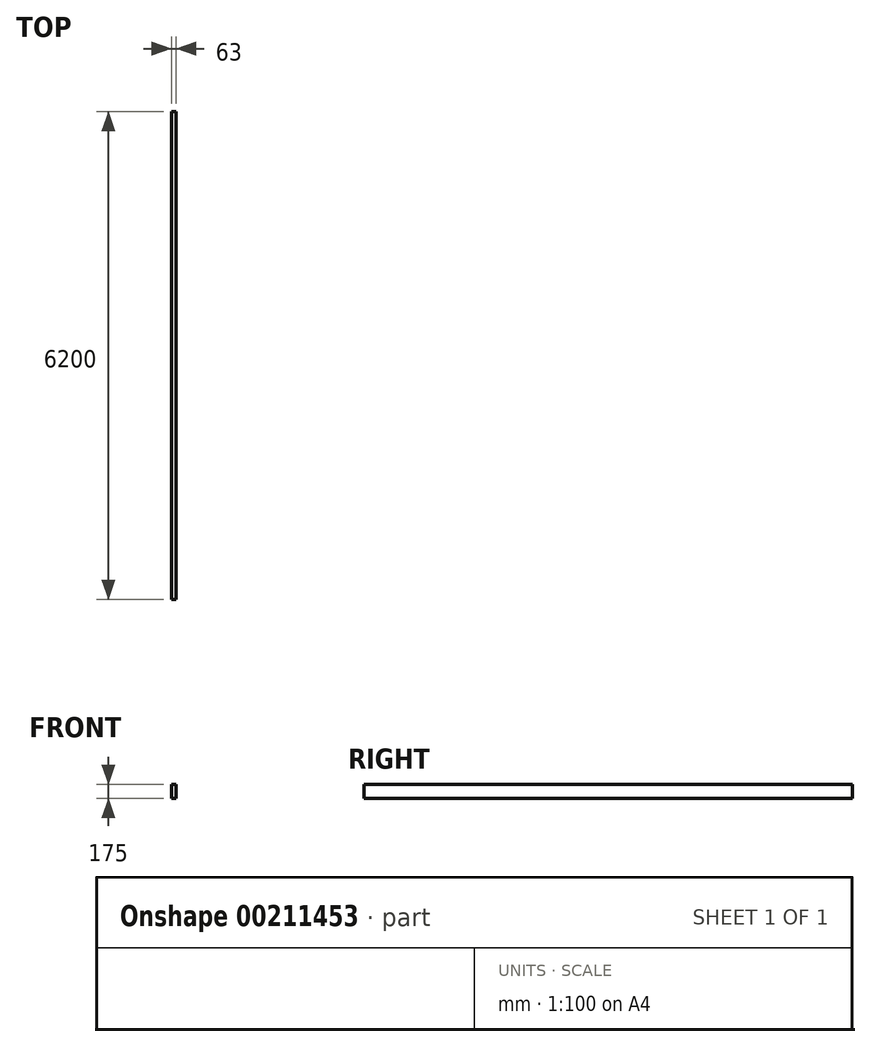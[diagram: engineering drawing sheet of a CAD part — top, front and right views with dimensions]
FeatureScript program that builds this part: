
annotation { "Feature Type Name" : "Feature", "Feature Type Description" : "" }
export const myFeature = defineFeature(function(context is Context, id is Id, definition is map)
    precondition{}
    {
        {
            var Q0;
            Q0=qCreatedBy(makeId("Front.planeOp"),FACE);
            var sketch = newSketch(context, id + "F0", { "sketchPlane" : qUnion([Q0])});
            skLineSegment(sketch, "E0.bottom", {"start": v(31.5, 87.5) * mm, "end": v(-31.5, 87.5) * mm});
            skLineSegment(sketch, "E0.top", {"start": v(31.5, -87.5) * mm, "end": v(-31.5, -87.5) * mm});
            skLineSegment(sketch, "E0.left", {"start": v(31.5, 87.5) * mm, "end": v(31.5, -87.5) * mm});
            skLineSegment(sketch, "E0.right", {"start": v(-31.5, 87.5) * mm, "end": v(-31.5, -87.5) * mm});
            skPoint(sketch, "E0.middle", {"position": v(0, 0) * mm});
            skSolve(sketch);
        }
        {
            var Q0;
            Q0=qSketchRegion(id+"F0",true);
            extrude(context, id + "F1", {"entities" : qUnion([Q0]), "depth" : 6200 * mm, "symmetric" : true});
        }
    });
